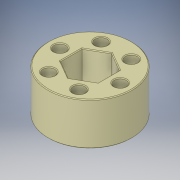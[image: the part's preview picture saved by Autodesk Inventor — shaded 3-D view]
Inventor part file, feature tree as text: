
AUTODESK INVENTOR PART (.ipt)
format: ipt  version: 2017.1 (Build 211199000, 199)  size: 174,080 bytes
history: native  units: in
note: dims shown in document units (in); Inventor stores cm internally (conversion verified against a paired STEP export)
features: extrude x3, chamfer x3, sketch x3, pattern_circular x1
ambient origin geometry x8: Origin, YZ Plane, XZ Plane, XY Plane, X Axis, Y Axis, Z Axis, Center Point
bodies: Solid1 (feature_tree)
feature tree (10):
  extrude  "Extrusion1"  Depth=0.57in TaperAngle=0.0deg
  extrude  "Extrusion2"  Depth=0.16in
  chamfer  "Chamfer1"  Distance=0.805in
  pattern_circular  "Circular Pattern1"  Count=6 Angle=360.0deg
  chamfer  "Chamfer2"  Distance=0.01in Angle=45.0deg
  extrude  "Extrusion3"  Depth=0.502in
  chamfer  "Chamfer3"  Distance=0.57in
  sketch  "Sketch1"  dims[d0=1.124in d1=0.57in d2=0.0in]
  sketch  "Sketch2"  dims[d3=0.81in d4=0.16in d5=0.805in d6=0.0in]
  sketch  "Sketch3"  dims[d7=0.01in d8=0.125in d9=45.0deg d10=2.3622in d11=360.0deg d13=0.01in d14=0.125in d15=45.0deg d16=0.502in d17=0.57in d18=0.0in d19=0.01in d20=0.125in d21=45.0deg]
